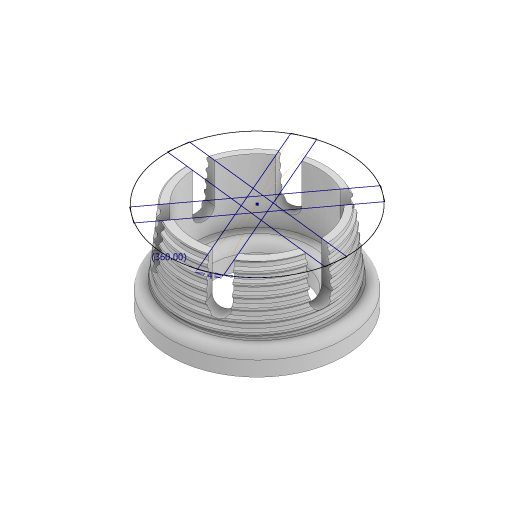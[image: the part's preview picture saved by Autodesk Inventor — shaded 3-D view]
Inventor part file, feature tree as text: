
AUTODESK INVENTOR PART (.ipt)
format: ipt  version: 2023 (Build 270158000, 158)  size: 994,304 bytes
history: native  units: mm
features: sketch x3, extrude x3, helix x2, fillet x2, revolve x1
ambient origin geometry x8: Origin, YZ Plane, XZ Plane, XY Plane, X Axis, Y Axis, Z Axis, Center Point
bodies: Solid1 (feature_tree)
feature tree (11):
  sketch  "Sketch2"  dims[d2=12.5mm d3=1.2mm d4=16.755161mm d5=90.0deg]
  revolve  "Revolution1"  [1 undecoded]
  helix  "Coil1"  [1 undecoded]
  helix  "Coil2"  [1 undecoded]
  sketch  "Sketch3"  dims[d6=12.875mm d7=2.0mm d8=12.875mm]
  extrude  "Extrusion1"  Depth=2.0mm
  extrude  "Extrusion2"  TaperAngle=90.0deg  [1 undecoded]
  extrude  "Extrusion3"  Depth=2.0mm
  fillet  "Fillet1"  [1 undecoded]
  fillet  "Fillet2"  Radius=4.0mm
  sketch  "Sketch4"  dims[d9=10.0mm d10=1.047198mm d11=90.0deg d12=90.0deg d13=0.0mm d14=0.0mm d15=2.0mm d16=2.0mm d17=10.0mm d18=-1.047198mm d19=90.0deg d20=90.0deg d21=0.0mm d22=0.0mm d23=4.0mm d24=30.0mm d26=360.0deg d28=0.0mm d29=0.0mm d30=10.0mm d31=0.0mm d32=5.0mm d33=0.0mm d34=2.0mm d35=2.0mm]
note: 5 required parameter values undecoded (feature->parameter linkage not recoverable at this tier; creation-order binding heuristic only, values carry confidence <= 0.55)